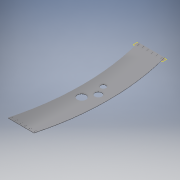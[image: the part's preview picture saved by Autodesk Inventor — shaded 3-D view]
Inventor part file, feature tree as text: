
AUTODESK INVENTOR PART (.ipt)
format: ipt  version: 2016 (Build 200138000, 138)  size: 152,576 bytes
history: native  units: mm
features: reference x29, extrude x3, sketch x3, plane x1
ambient origin geometry x8: Origin, YZ Plane, XZ Plane, XY Plane, X Axis, Y Axis, Z Axis, Center Point
bodies: Solid1 (feature_tree)
feature tree (36):
  plane  "Work Plane1"
  extrude  "Extrusion1"  Depth=5.0mm TaperAngle=0.0deg
  extrude  "Extrusion2"  Depth=10.0mm
  extrude  "Extrusion3"  Depth=5.0mm
  sketch  "Sketch1"  dims[d0=5.0mm d1=0.0mm d2=5.0mm d3=0.0mm]
  reference  "Reference1"
  reference  "Reference2"
  reference  "Reference3"
  reference  "Reference4"
  sketch  "Sketch2"  dims[d8=10.0mm d9=100.0mm]
  reference  "Reference5"
  reference  "Reference6"
  reference  "Reference7"
  reference  "Reference8"
  reference  "Reference9"
  reference  "Reference10"
  reference  "Reference11"
  reference  "Reference12"
  reference  "Reference13"
  reference  "Reference14"
  reference  "Reference15"
  reference  "Reference16"
  reference  "Reference17"
  reference  "Reference18"
  reference  "Reference19"
  reference  "Reference20"
  reference  "Reference21"
  reference  "Reference22"
  reference  "Reference23"
  reference  "Reference24"
  reference  "Reference25"
  reference  "Reference26"
  reference  "Reference27"
  reference  "Reference28"
  sketch  "Sketch3"  dims[d10=80.0mm d11=60.0mm d12=50.0mm d13=5.0mm d14=0.0mm]
  reference  "Reference29"
